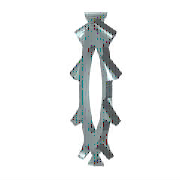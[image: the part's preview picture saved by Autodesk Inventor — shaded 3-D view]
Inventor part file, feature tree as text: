
AUTODESK INVENTOR PART (.ipt)
format: ipt  version: 2017 (Build 210142000, 142)  size: 178,688 bytes
history: native  units: mm (DEFAULTED — no unit token found)
features: extrude x2, sketch x2, pattern_circular x1, other x1, plane x1
ambient origin geometry x7: Origin, YZ Plane, XY Plane, X Axis, Y Axis, Z Axis, Center Point
bodies: Solid1 (feature_tree)
feature tree (7):
  extrude  "Базовый элемент"  Depth=20.5mm
  extrude  "Вырез"  Depth=13.0mm
  pattern_circular  "Вырезы"  [2 undecoded]
  other  "Work Axis1"
  plane  "Work Plane1"
  sketch  "Эскиз1"
  sketch  "Эскиз2"
note: 2 required parameter values undecoded (feature->parameter linkage not recoverable at this tier; creation-order binding heuristic only, values carry confidence <= 0.55)
